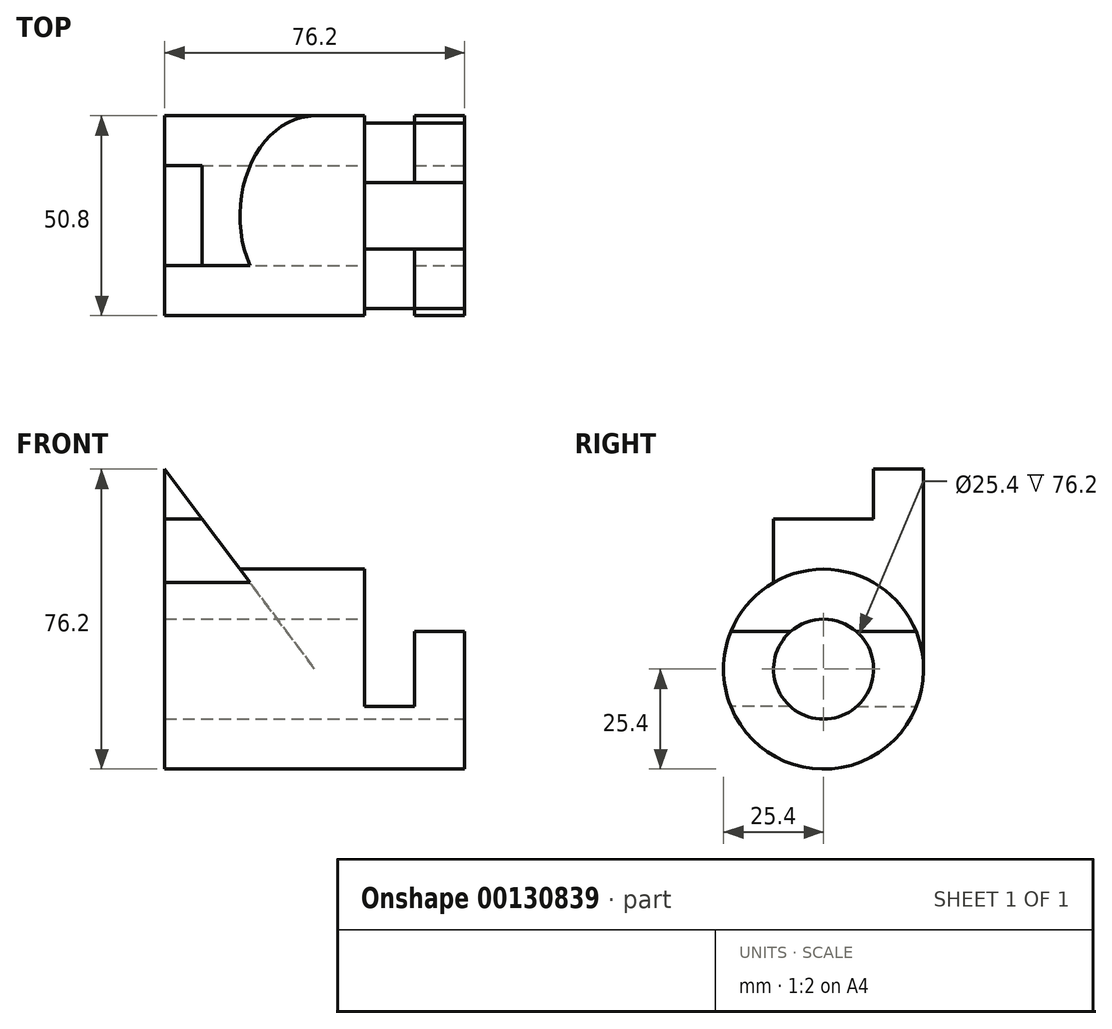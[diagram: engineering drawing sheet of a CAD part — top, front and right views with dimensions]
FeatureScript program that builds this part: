
annotation { "Feature Type Name" : "Feature", "Feature Type Description" : "" }
export const myFeature = defineFeature(function(context is Context, id is Id, definition is map)
    precondition{}
    {
        {
            var Q0;
            Q0=qCreatedBy(makeId("Right.planeOp"),FACE);
            var sketch = newSketch(context, id + "F0", { "sketchPlane" : qUnion([Q0])});
            skCircle(sketch, "E0", {"center": v(0, 0) * mm, "radius": 25.4 * mm});
            skSolve(sketch);
        }
        {
            var Q0;
            Q0 = qSketchRegion(id + "F0", true);
            extrude(context, id + "F1", {"entities" : qUnion([Q0]), "oppositeDirection" : true, "depth" : 76.2 * mm});
        }
        {
            var Q0;
            Q0=makeQuery(id+"F1.opExtrude","CAP_FACE",FACE,{"disambiguationData":[OSD([sQuery(id+"F0.wireOp",EDGE,"E0")])],"isStart":true});
            var sketch = newSketch(context, id + "F2", { "sketchPlane" : qUnion([Q0])});
            skLineSegment(sketch, "E1", {"start": v(-23.55, 9.53) * mm, "end": v(23.55, 9.53) * mm});
            skArc(sketch, "E2.0", {"start": v(23.55, 9.53) * mm, "mid": v(0, 25.4) * mm, "end": v(-23.55, 9.53) * mm});
            skSolve(sketch);
        }
        {
            var Q0;
            Q0 = qSketchRegion(id + "F2", true);
            extrude(context, id + "F3", {"entities" : qUnion([Q0]), "operationType" : NewBodyOperationType.REMOVE, "oppositeDirection" : true, "depth" : 25.4 * mm});
        }
        {
            var Q0;
            Q0=makeQuery(id+"F3.boolean.opBoolean","COPY",FACE,{"derivedFrom":makeQuery(id+"F3.opExtrude","SWEPT_FACE",FACE,{"disambiguationData":[OSD([sQuery(id+"F2.wireOp",EDGE,"E1")])]})});
            var sketch = newSketch(context, id + "F4", { "sketchPlane" : qUnion([Q0])});
            skLineSegment(sketch, "E3", {"start": v(-25.4, 25.4) * mm, "end": v(-12.7, 25.4) * mm});
            skLineSegment(sketch, "E4", {"start": v(-12.7, -25.4) * mm, "end": v(-25.4, -25.4) * mm});
            skLineSegment(sketch, "E5", {"start": v(-25.4, 25.4) * mm, "end": v(-25.4, -25.4) * mm});
            skLineSegment(sketch, "E6", {"start": v(-25.4, -25.4) * mm, "end": v(-12.7, -25.4) * mm});
            skLineSegment(sketch, "E7", {"start": v(-12.7, -25.4) * mm, "end": v(-12.7, 25.4) * mm});
            skLineSegment(sketch, "E8", {"start": v(-12.7, 25.4) * mm, "end": v(-25.4, 25.4) * mm});
            skSolve(sketch);
        }
        {
            var Q0;
            Q0 = qSketchRegion(id + "F4", true);
            extrude(context, id + "F5", {"entities" : qUnion([Q0]), "operationType" : NewBodyOperationType.REMOVE, "oppositeDirection" : true, "depth" : 19.05 * mm});
        }
        {
            var Q0;
            Q0=qCreatedBy(makeId("Front.planeOp"),FACE);
            var sketch = newSketch(context, id + "F6", { "sketchPlane" : qUnion([Q0])});
            skLineSegment(sketch, "E9", {"start": v(-38.1, 0) * mm, "end": v(-76.2, 50.8) * mm});
            skLineSegment(sketch, "E10", {"start": v(-76.2, 50.8) * mm, "end": v(-76.2, -25.4) * mm});
            skLineSegment(sketch, "E11", {"start": v(-76.2, -25.4) * mm, "end": v(0, -25.4) * mm});
            skLineSegment(sketch, "E12", {"start": v(-54.77, 22.23) * mm, "end": v(-76.2, 22.23) * mm});
            skLineSegment(sketch, "E13.0", {"start": v(0, 9.52) * mm, "end": v(0, -25.4) * mm});
            skLineSegment(sketch, "E14", {"start": v(-38.1, 0) * mm, "end": v(-76.2, 0) * mm});
            skSolve(sketch);
        }
        {
            var Q0;
            Q0 = qSketchRegion(id + "F6", true);
            extrude(context, id + "F7", {"entities" : qUnion([Q0]), "operationType" : NewBodyOperationType.ADD, "endBound" : BoundingType.SYMMETRIC, "depth" : 50.8 * mm});
        }
        {
            var Q0;
            Q0=qCreatedBy(makeId("Right.planeOp"),FACE);
            var sketch = newSketch(context, id + "F8", { "sketchPlane" : qUnion([Q0])});
            skCircle(sketch, "E15", {"center": v(0, 0) * mm, "radius": 12.7 * mm});
            skSolve(sketch);
        }
        {
            var Q0;
            Q0 = qSketchRegion(id + "F8", true);
            extrude(context, id + "F9", {"entities" : qUnion([Q0]), "operationType" : NewBodyOperationType.REMOVE, "endBound" : BoundingType.THROUGH_ALL, "oppositeDirection" : true, "depth" : 25.4 * mm});
        }
        {
            var Q0;
            Q0=makeQuery(id+"F1.opExtrude","CAP_FACE",FACE,{"disambiguationData":[OSD([sQuery(id+"F0.wireOp",EDGE,"E0")])],"isStart":true});
            var sketch = newSketch(context, id + "F10", { "sketchPlane" : qUnion([Q0])});
            skArc(sketch, "E16.0", {"start": v(-12.7, 22) * mm, "mid": v(-24.02, 8.26) * mm, "end": v(-23.55, -9.52) * mm});
            skLineSegment(sketch, "E17.0", {"start": v(-25.4, 0) * mm, "end": v(-25.4, 50.8) * mm});
            skLineSegment(sketch, "E18.0", {"start": v(-25.4, 50.8) * mm, "end": v(-12.7, 50.8) * mm});
            skLineSegment(sketch, "E19", {"start": v(-12.7, 22) * mm, "end": v(-12.7, 50.8) * mm});
            skPoint(sketch, "E20.orphan", {"position": v(25.4, 50.8) * mm});
            skPoint(sketch, "E21.orphan", {"position": v(23.55, -9.53) * mm});
            skSolve(sketch);
        }
        {
            var Q0;
            Q0 = qSketchRegion(id + "F10", true);
            extrude(context, id + "F11", {"entities" : qUnion([Q0]), "operationType" : NewBodyOperationType.REMOVE, "endBound" : BoundingType.THROUGH_ALL, "oppositeDirection" : true, "depth" : 25.4 * mm});
        }
        {
            var Q0;
            Q0=makeQuery(id+"F1.opExtrude","CAP_FACE",FACE,{"disambiguationData":[OSD([sQuery(id+"F0.wireOp",EDGE,"E0")])],"isStart":true});
            var sketch = newSketch(context, id + "F12", { "sketchPlane" : qUnion([Q0])});
            skLineSegment(sketch, "E22.0", {"start": v(-12.7, 50.8) * mm, "end": v(12.7, 50.8) * mm});
            skLineSegment(sketch, "E23.0", {"start": v(-12.7, 50.8) * mm, "end": v(-12.7, 38.1) * mm});
            skLineSegment(sketch, "E24", {"start": v(-12.7, 38.1) * mm, "end": v(12.7, 38.1) * mm});
            skLineSegment(sketch, "E25", {"start": v(12.7, 38.1) * mm, "end": v(12.7, 50.8) * mm});
            skPoint(sketch, "E26.orphan", {"position": v(-12.7, 22) * mm});
            skPoint(sketch, "E27.orphan", {"position": v(25.4, 50.8) * mm});
            skSolve(sketch);
        }
        {
            var Q0;
            Q0 = qSketchRegion(id + "F12", true);
            extrude(context, id + "F13", {"entities" : qUnion([Q0]), "operationType" : NewBodyOperationType.REMOVE, "endBound" : BoundingType.THROUGH_ALL, "oppositeDirection" : true, "depth" : 25.4 * mm});
        }
    });
